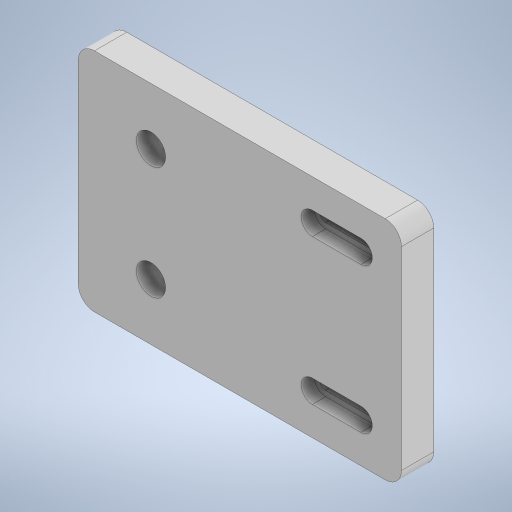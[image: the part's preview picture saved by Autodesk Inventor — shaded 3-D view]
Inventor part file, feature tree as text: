
AUTODESK INVENTOR PART (.ipt)
format: ipt  version: 2023 (Build 270158000, 158)  size: 261,120 bytes
history: native  units: mm
features: sketch x4, extrude x3, hole x2, other x1, fillet x1
ambient origin geometry x8: Origin, YZ Plane, XZ Plane, XY Plane, X Axis, Y Axis, Z Axis, Center Point
bodies: Body1 (feature_tree)
feature tree (11):
  other  "Těleso1"
  extrude  "Vysunutí1"  Depth=70.0mm
  fillet  "Zaoblení1"  Radius=100.0mm
  hole  "Díra1"  [1 undecoded]
  sketch  "Náčrt3"
  hole  "Díra2"  [1 undecoded]
  extrude  "Vysunutí2"  Depth=22.5mm
  extrude  "Vysunutí3"  Depth=22.5mm
  sketch  "Náčrt1"
  sketch  "Náčrt2"
  sketch  "Náčrt4"
note: 2 required parameter values undecoded (feature->parameter linkage not recoverable at this tier; creation-order binding heuristic only, values carry confidence <= 0.55)
